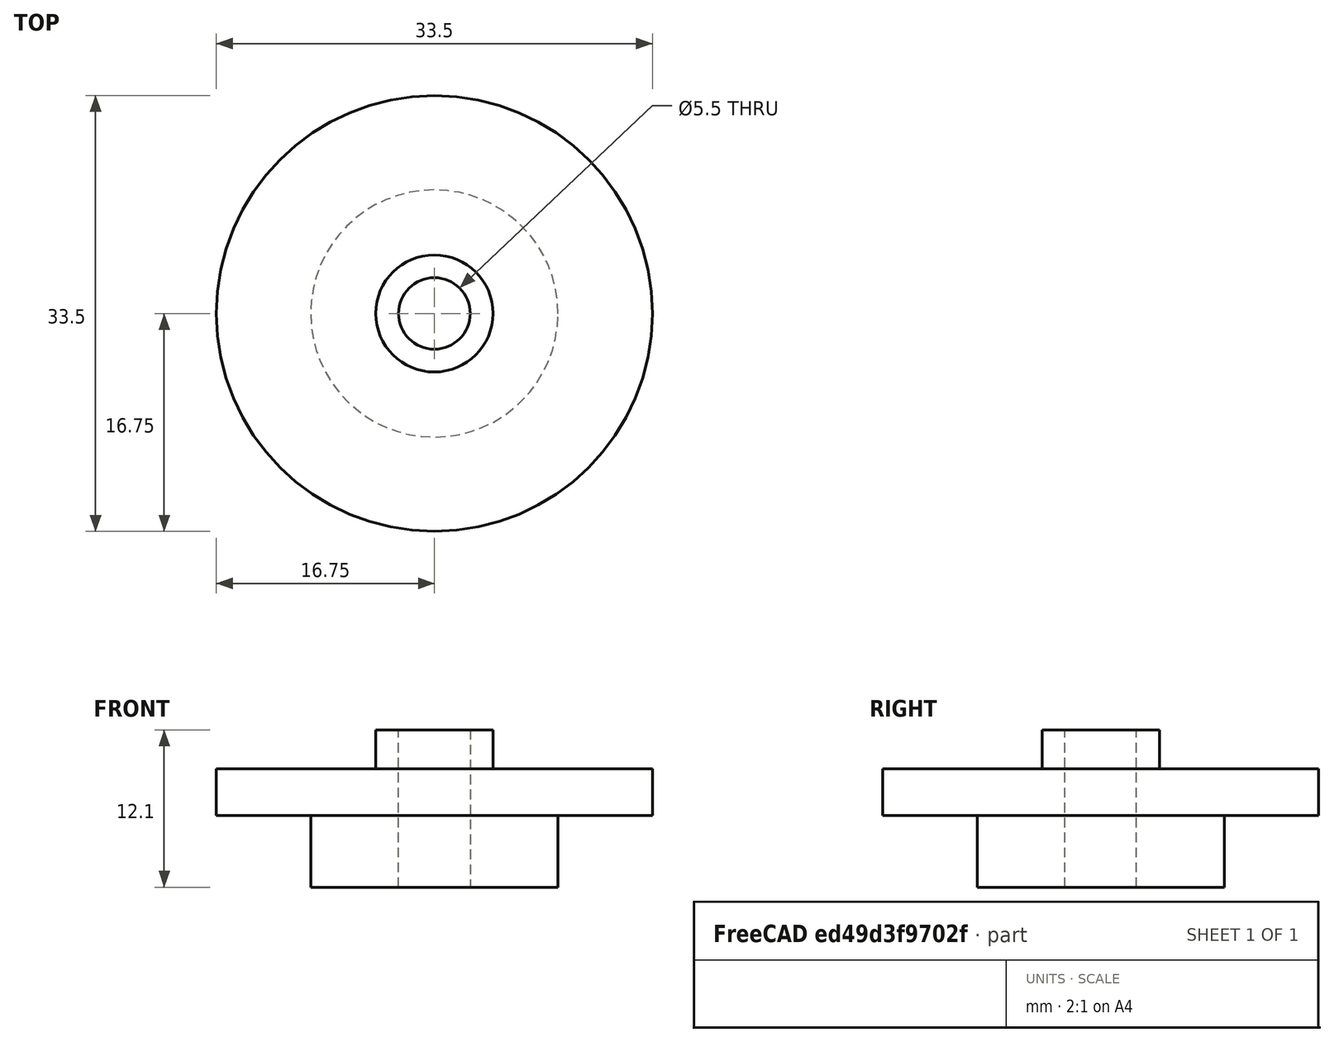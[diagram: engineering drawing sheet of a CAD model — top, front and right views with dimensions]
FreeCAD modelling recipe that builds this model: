
FCSTD DOCUMENT  (FreeCAD 0.18R16110 (Git))
Label: gear1_5.5x33.5
License: All rights reserved
LicenseURL: http://en.wikipedia.org/wiki/All_rights_reserved
objects: Sketcher::SketchObject×4, PartDesign::Pad×3, PartDesign::Body×1, PartDesign::Pocket×1
note: 13 computed .brp shape members not serialized (recipe doc carries the construction recipe); baked Part::Feature solids carry a one-line shape summary decoded from their .brp

FEATURE [Sketcher::SketchObject] Sketch
  MapMode = 5
  Support = -> [XY_Plane]
  sketch-geometry (1):
    g0: Circle CenterX=0 CenterY=0 CenterZ=0 NormalX=0 NormalY=0 NormalZ=1 AngleXU=0 Radius=16.75
  constraints (2):
    c: Coincident(g0,g-1)
    c: Diameter(g0) = 33.5
FEATURE [PartDesign::Pad] Pad
  Length = 3.6
  Length2 = 100
  Profile = -> Sketch
  Type = 0
FEATURE [Sketcher::SketchObject] Sketch001
  MapMode = 5
  Placement = pos=(0,0,3.6) rot=(0,0,1;0rad)
  Support = -> [Pad]
  sketch-geometry (1):
    g0: Circle CenterX=0 CenterY=0 CenterZ=0 NormalX=0 NormalY=0 NormalZ=1 AngleXU=0 Radius=4.5
  constraints (2):
    c: Coincident(g0,g-1)
    c: Diameter(g0) = 9
FEATURE [PartDesign::Body] Body
  Group = -> [Sketch,Pad,Sketch001,Sketch002,Sketch003,Pad002,Pad001,Pocket]
  Origin = -> Origin
  Tip = -> Pocket
FEATURE [PartDesign::Pad] Pad001
  BaseFeature = -> Pad002
  Length = 3
  Length2 = 100
  Profile = -> Sketch001
  Type = 0
FEATURE [Sketcher::SketchObject] Sketch002
  MapMode = 5
  Placement = pos=(0,0,6.6) rot=(0,0,1;0rad)
  Support = -> [Pad001]
  sketch-geometry (1):
    g0: Circle CenterX=0 CenterY=0 CenterZ=0 NormalX=0 NormalY=0 NormalZ=1 AngleXU=0 Radius=2.75
  constraints (2):
    c: Coincident(g-1,g0)
    c: Diameter(g0) = 5.5
FEATURE [PartDesign::Pocket] Pocket
  BaseFeature = -> Pad001
  Length = 5
  Length2 = 100
  Profile = -> Sketch002
  Type = 1
FEATURE [Sketcher::SketchObject] Sketch003
  MapMode = 5
  Placement = pos=(0,0,0) rot=(1,0,0;3.14159rad)
  Support = -> [Pocket]
  sketch-geometry (1):
    g0: Circle CenterX=0 CenterY=0 CenterZ=0 NormalX=0 NormalY=0 NormalZ=1 AngleXU=0 Radius=9.5
  constraints (2):
    c: Coincident(g0,g-1)
    c: Diameter(g0) = 19
FEATURE [PartDesign::Pad] Pad002
  BaseFeature = -> Pad
  Length = 5.5
  Length2 = 100
  Profile = -> Sketch003
  Type = 0
